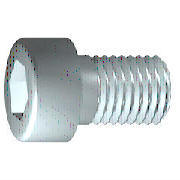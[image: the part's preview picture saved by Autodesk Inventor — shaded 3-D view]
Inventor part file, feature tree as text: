
AUTODESK INVENTOR PART (.ipt)
format: ipt  version: 2024 (Build 280153000, 153)  size: 199,168 bytes
history: native  units: mm (DEFAULTED — no unit token found)
features: extrude x1, plane x1, fillet x1
ambient origin geometry x7: Origin, YZ Plane, XY Plane, X Axis, Y Axis, Z Axis, Center Point
bodies: Solid1 (feature_tree), Body (feature_tree)
feature tree (3):
  extrude  "Slot"  Depth=10.75mm
  plane  "Work Plane1"
  fillet  "Fillet2"  Radius=0.306825mm
